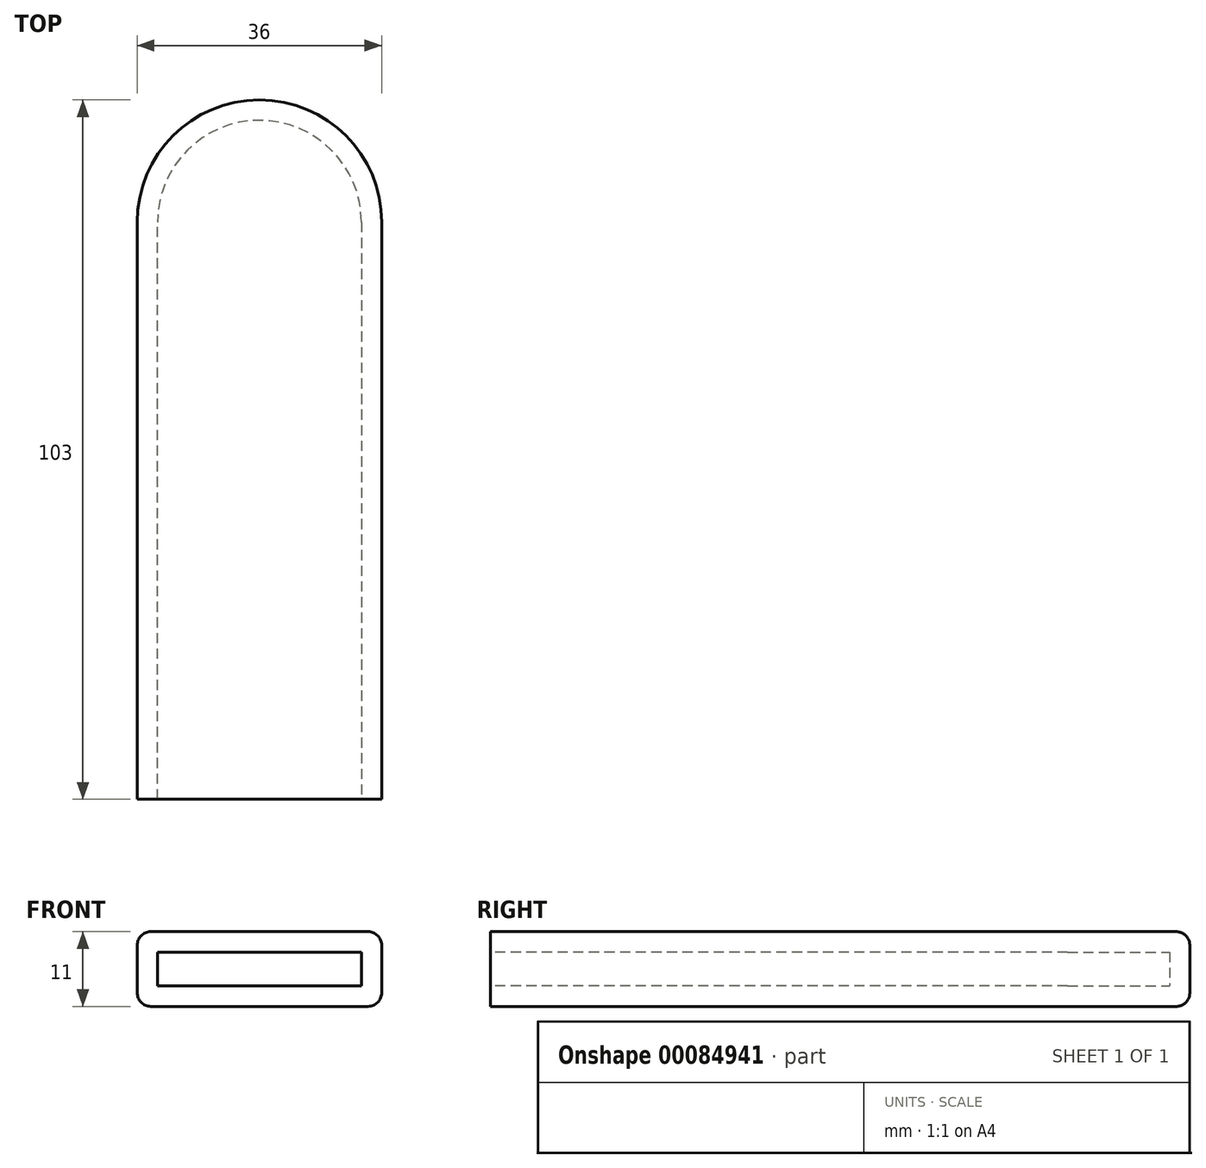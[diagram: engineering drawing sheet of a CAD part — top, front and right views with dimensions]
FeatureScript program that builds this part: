
annotation { "Feature Type Name" : "Feature", "Feature Type Description" : "" }
export const myFeature = defineFeature(function(context is Context, id is Id, definition is map)
    precondition{}
    {
        {
            var Q0;
            Q0=qCreatedBy(makeId("Top.planeOp"),FACE);
            var sketch = newSketch(context, id + "F0", { "sketchPlane" : qUnion([Q0])});
            skLineSegment(sketch, "E0", {"start": v(21.99, 63.07) * mm, "end": v(21.99, -21.93) * mm});
            skLineSegment(sketch, "E1", {"start": v(21.99, -21.93) * mm, "end": v(-14.01, -21.93) * mm});
            skLineSegment(sketch, "E2", {"start": v(-14.01, -21.93) * mm, "end": v(-14.01, 63.07) * mm});
            skArc(sketch, "E3", {"start": v(-14.01, 63.07) * mm, "mid": v(3.99, 81.07) * mm, "end": v(21.99, 63.07) * mm});
            skSolve(sketch);
        }
        {
            var Q0;
            Q0=makeQuery(id+"F0.imprint","IMPRINT",FACE,{"disambiguationData":[TD([[makeQuery(id+"F0.imprint","IMPRINT",EDGE,{"derivedFrom":sQuery(id+"F0.wireOp",EDGE,"E0")}),-1.0]])]});
            extrude(context, id + "F1", {"entities" : qUnion([Q0]), "depth" : 11 * mm});
        }
        {
            var Q0;
            Q0=makeQuery(id+"F1.opExtrude","SWEPT_FACE",FACE,{"disambiguationData":[OSD([sQuery(id+"F0.wireOp",EDGE,"E1")])]});
            shell(context, id + "F2", {"entities" : qUnion([Q0]), "thickness" : 3 * mm});
        }
        {
            var Q0;
            Q0=makeQuery(id+"F1.opExtrude","CAP_EDGE",EDGE,{"disambiguationData":[OSD([sQuery(id+"F0.wireOp",EDGE,"E2")])],"isStart":false});
            var Q1;
            Q1=makeQuery(id+"F1.opExtrude","CAP_EDGE",EDGE,{"disambiguationData":[OSD([sQuery(id+"F0.wireOp",EDGE,"E3")])],"isStart":false});
            var Q2;
            Q2=makeQuery(id+"F1.opExtrude","CAP_EDGE",EDGE,{"disambiguationData":[OSD([sQuery(id+"F0.wireOp",EDGE,"E0")])],"isStart":false});
            fillet(context, id + "F3", {"entities" : qUnion([Q0, Q1, Q2]), "radius" : 2 * mm, "tangentPropagation" : true, "allowEdgeOverflow" : false});
        }
        {
            var Q0;
            Q0=makeQuery(id+"F1.opExtrude","CAP_EDGE",EDGE,{"disambiguationData":[OSD([sQuery(id+"F0.wireOp",EDGE,"E2")])],"isStart":true});
            var Q1;
            Q1=makeQuery(id+"F1.opExtrude","CAP_EDGE",EDGE,{"disambiguationData":[OSD([sQuery(id+"F0.wireOp",EDGE,"E0")])],"isStart":true});
            var Q2;
            Q2=makeQuery(id+"F1.opExtrude","CAP_EDGE",EDGE,{"disambiguationData":[OSD([sQuery(id+"F0.wireOp",EDGE,"E3")])],"isStart":true});
            fillet(context, id + "F4", {"entities" : qUnion([Q0, Q1, Q2]), "radius" : 2 * mm, "tangentPropagation" : true, "allowEdgeOverflow" : false});
        }
    });
